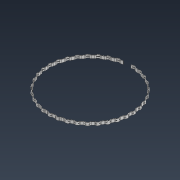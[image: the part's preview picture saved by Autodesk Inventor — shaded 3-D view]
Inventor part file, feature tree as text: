
AUTODESK INVENTOR PART (.ipt)
format: ipt  version: 2022 (Build 260153000, 153)  size: 1,343,488 bytes
history: native  units: mm
features: sketch x3, extrude x1, plane x1, revolve x1
ambient origin geometry x8: Origin, YZ Plane, XZ Plane, XY Plane, X Axis, Y Axis, Z Axis, Center Point
bodies: Solid1 (feature_tree)
feature tree (6):
  extrude  "Extrusion1"  Depth=85.0mm
  plane  "Work Plane1"
  sketch  "Sketch5"  dims[d17=2.0mm d19=0.5mm]
  revolve  "Revolution1"  [1 undecoded]
  sketch  "Sketch2"  dims[d14=83.0mm d15=85.0mm]
  sketch  "Sketch6"  dims[d20=340.0mm d22=59.341195mm d24=3.0mm d25=0.0mm d26=0.5mm d28=360.0deg d30=0.1mm d31=0.5mm d32=0.4mm]
note: 1 required parameter value undecoded (feature->parameter linkage not recoverable at this tier; creation-order binding heuristic only, values carry confidence <= 0.55)
